# Revit family: CSensor-Lutron-Ceiling-QS_Series-QSM2-4W-C
name_source: partatom
category: Lighting Devices
units: mm (PartAtom-declared; Revit-internal decimal feet)

## family parameters
Cut with Voids When Loaded = No
Host = Face
Maintain Annotation Orientation = Yes
OmniClass Number = 23.85.80.11.27
OmniClass Title = Lighting Controls
Part Type = Normal
Room Calculation Point = No
Round Connector Dimension = Use Diameter
Shared = No

## types (1)
- QSM2-4W-C
    Assembly Code = D5030800
    Cost = 0 $
    Coverage = 2827.00 SF
    Coverage Area = 360˚ coverage ranges from 60 ft (18 m) line of sight to 30 ft (9 m) through walls
    Coverage Range = 60 ft (18 m) line of sight - 30 ft (9 m) through walls
    Coverge Radius = 30' - 0"
    Default Elevation = 0' - 0"
    Depth = 0' - 1 11/64"
    Description = Ceiling-mounted device that integrates Lutron wireless and wired sensors and controls through the QS communication link.
    Finish = Plastic - Lutron - White Gloss
    Instruction Sheet Link = https://assets.lutron.com
    Keynote = Division 11
    Length = 0' - 4 5/128"
    Manufacturer = Lutron Electronics Co., Inc
    Manufacturer Fax Number = 610-282-1243
    Maximum Operating Temperature = 104 °F
    Minimum Operating Temperature = 32 °F
    Model = QSM2-4W-C
    Performance URL = https://www.lutron.com
    Product Documentation Link = https://assets.lutron.com
    Product Name = QS Sensor Module
    Product Page URL = https://www.lutron.com
    Sensor Material = Plastic - Lutron - White Gloss
    Sensor Type = Occupancy/Vacancy
    Series = QS Series
    URL = http://www.lutron.com
    Version = 2021 - v1.0a
    Video Link = https://www.youtube.com
    Voltage = 0 V
    Voltage Comments = No line voltage connections are required because the QSM is powered by the QS Link.
    Warranty URL = https://www.lutron.com
    Width = 0' - 4 5/128"

## geometry (parser evidence)
native form markers: Sweep x5
no freeform markers — native parametric forms only
